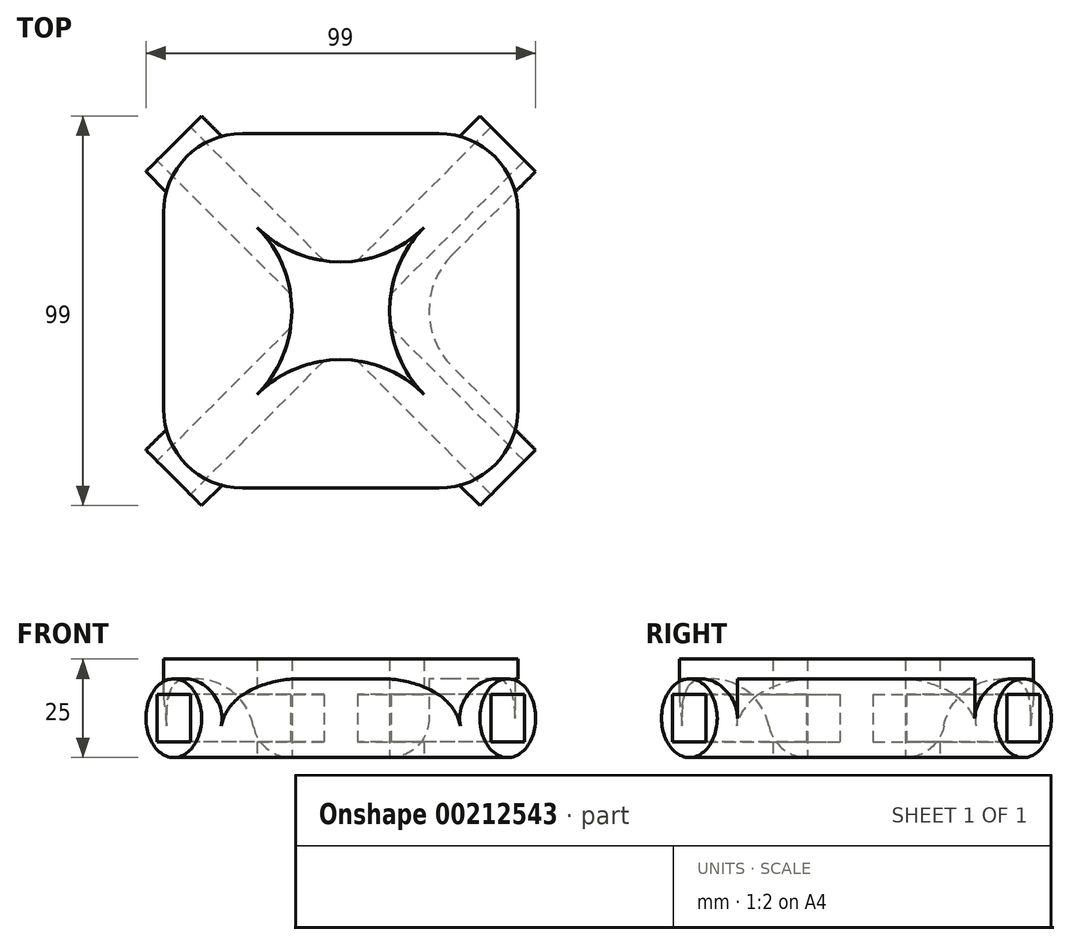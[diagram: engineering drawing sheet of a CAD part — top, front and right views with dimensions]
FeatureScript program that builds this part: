
annotation { "Feature Type Name" : "Feature", "Feature Type Description" : "" }
export const myFeature = defineFeature(function(context is Context, id is Id, definition is map)
    precondition{}
    {
        {
            var Q0;
            Q0=qCreatedBy(makeId("Top.planeOp"),FACE);
            var sketch = newSketch(context, id + "F0", { "sketchPlane" : qUnion([Q0])});
            skLineSegment(sketch, "E0.bottom", {"start": v(25, 45) * mm, "end": v(-25, 45) * mm});
            skLineSegment(sketch, "E0.top", {"start": v(25, -45) * mm, "end": v(-25, -45) * mm});
            skLineSegment(sketch, "E0.left", {"start": v(45, 25) * mm, "end": v(45, -25) * mm});
            skLineSegment(sketch, "E0.right", {"start": v(-45, 25) * mm, "end": v(-45, -25) * mm});
            skPoint(sketch, "E0.middle", {"position": v(0, 0) * mm});
            skPoint(sketch, "E1.visualSharp", {"position": v(-45, 45) * mm});
            skArc(sketch, "E1.filletArc", {"start": v(-25, 45) * mm, "mid": v(-39.14, 39.14) * mm, "end": v(-45, 25) * mm});
            skPoint(sketch, "E2.visualSharp", {"position": v(45, 45) * mm});
            skArc(sketch, "E2.filletArc", {"start": v(45, 25) * mm, "mid": v(39.14, 39.14) * mm, "end": v(25, 45) * mm});
            skPoint(sketch, "E3.visualSharp", {"position": v(45, -45) * mm});
            skArc(sketch, "E3.filletArc", {"start": v(25, -45) * mm, "mid": v(39.14, -39.14) * mm, "end": v(45, -25) * mm});
            skPoint(sketch, "E4.visualSharp", {"position": v(-45, -45) * mm});
            skArc(sketch, "E4.filletArc", {"start": v(-45, -25) * mm, "mid": v(-39.14, -39.14) * mm, "end": v(-25, -45) * mm});
            skSolve(sketch);
        }
        {
            var Q0;
            Q0=qCreatedBy(makeId("Top.planeOp"),FACE);
            cPlane(context, id + "F1", {"entities" : qUnion([Q0]), "cplaneType" : CPlaneType.OFFSET, "offset" : 20 * mm, "oppositeDirection" : true, "width" : 150 * mm, "height" : 150 * mm});
        }
        {
            var Q0;
            Q0=qCreatedBy(id+"F1.planeOp",FACE);
            var sketch = newSketch(context, id + "F2", { "sketchPlane" : qUnion([Q0])});
            skLineSegment(sketch, "E5", {"start": v(-42.43, -42.43) * mm, "end": v(42.43, 42.43) * mm, "construction": true});
            skLineSegment(sketch, "E6", {"start": v(-42.43, 42.43) * mm, "end": v(42.43, -42.43) * mm, "construction": true});
            skLineSegment(sketch, "E7", {"start": v(0, 0) * mm, "end": v(0, -45) * mm, "construction": true});
            skLineSegment(sketch, "E8.bottom", {"start": v(-49.5, -35.36) * mm, "end": v(-35.36, -49.5) * mm});
            skLineSegment(sketch, "E8.top", {"start": v(35.36, 49.5) * mm, "end": v(49.5, 35.36) * mm});
            skLineSegment(sketch, "E8.left", {"start": v(-49.5, -35.36) * mm, "end": v(-28.28, -14.14) * mm});
            skLineSegment(sketch, "E8.right", {"start": v(-35.36, -49.5) * mm, "end": v(-14.14, -28.28) * mm});
            skPoint(sketch, "E8.middle", {"position": v(0, 0) * mm});
            skLineSegment(sketch, "E9.bottom", {"start": v(49.5, -35.36) * mm, "end": v(28.28, -14.14) * mm});
            skLineSegment(sketch, "E9.top", {"start": v(35.36, -49.5) * mm, "end": v(14.14, -28.28) * mm});
            skLineSegment(sketch, "E9.left", {"start": v(35.36, -49.5) * mm, "end": v(49.5, -35.36) * mm});
            skLineSegment(sketch, "E9.right", {"start": v(-49.5, 35.36) * mm, "end": v(-35.36, 49.5) * mm});
            skLineSegment(sketch, "E10.trimOffspring", {"start": v(14.14, 28.28) * mm, "end": v(35.36, 49.5) * mm});
            skLineSegment(sketch, "E11.trimOffspring", {"start": v(-28.28, 14.14) * mm, "end": v(-49.5, 35.36) * mm});
            skLineSegment(sketch, "E12.trimOffspring", {"start": v(28.28, 14.14) * mm, "end": v(49.5, 35.36) * mm});
            skLineSegment(sketch, "E13.trimOffspring", {"start": v(-14.14, 28.28) * mm, "end": v(-35.36, 49.5) * mm});
            skPoint(sketch, "E14.visualSharp", {"position": v(0, -14.14) * mm});
            skArc(sketch, "E14.filletArc", {"start": v(14.14, -28.28) * mm, "mid": v(0, -22.43) * mm, "end": v(-14.14, -28.28) * mm});
            skPoint(sketch, "E15.visualSharp", {"position": v(-14.14, 0) * mm});
            skArc(sketch, "E15.filletArc", {"start": v(-28.28, -14.14) * mm, "mid": v(-22.43, 0) * mm, "end": v(-28.28, 14.14) * mm});
            skPoint(sketch, "E16.visualSharp", {"position": v(14.14, 0) * mm});
            skArc(sketch, "E16.filletArc", {"start": v(28.28, 14.14) * mm, "mid": v(22.43, 0) * mm, "end": v(28.28, -14.14) * mm});
            skPoint(sketch, "E17.visualSharp", {"position": v(0, 14.14) * mm});
            skArc(sketch, "E17.filletArc", {"start": v(-14.14, 28.28) * mm, "mid": v(0, 22.43) * mm, "end": v(14.14, 28.28) * mm});
            skSolve(sketch);
        }
        {
            var Q0;
            Q0=makeQuery(id+"F0.imprint","IMPRINT",FACE,{"disambiguationData":[TD([[makeQuery(id+"F0.imprint","IMPRINT",EDGE,{"derivedFrom":sQuery(id+"F0.wireOp",EDGE,"E0.bottom")}),1.0]])]});
            extrude(context, id + "F3", {"entities" : qUnion([Q0]), "depth" : 5 * mm});
        }
        {
            var Q0;
            Q0=makeQuery(id+"F2.imprint","IMPRINT",FACE,{"disambiguationData":[TD([[makeQuery(id+"F2.imprint","IMPRINT",EDGE,{"derivedFrom":sQuery(id+"F2.wireOp",EDGE,"E8.bottom")}),1.0]])]});
            var Q1;
            Q1=makeQuery(id+"F3.opExtrude","CAP_FACE",FACE,{"disambiguationData":[OSD([sQuery(id+"F0.wireOp",EDGE,"E0.bottom"),sQuery(id+"F0.wireOp",EDGE,"E0.top"),sQuery(id+"F0.wireOp",EDGE,"E0.left"),sQuery(id+"F0.wireOp",EDGE,"E0.right"),sQuery(id+"F0.wireOp",EDGE,"E1.filletArc"),sQuery(id+"F0.wireOp",EDGE,"E2.filletArc"),sQuery(id+"F0.wireOp",EDGE,"E3.filletArc"),sQuery(id+"F0.wireOp",EDGE,"E4.filletArc")])],"isStart":true});
            extrude(context, id + "F4", {"entities" : qUnion([Q0]), "operationType" : NewBodyOperationType.ADD, "endBound" : BoundingType.UP_TO_SURFACE, "endBoundEntityFace" : qUnion([Q1]), "depth" : 25 * mm});
        }
        {
            var Q0;
            Q0=makeQuery(id+"F4.opExtrude","CAP_EDGE",EDGE,{"disambiguationData":[OSD([sQuery(id+"F2.wireOp",EDGE,"E9.bottom")])],"isStart":true});
            var Q1;
            Q1=makeQuery(id+"F4.opExtrude","CAP_EDGE",EDGE,{"disambiguationData":[OSD([sQuery(id+"F2.wireOp",EDGE,"E14.filletArc")])],"isStart":true});
            var Q2;
            Q2=makeQuery(id+"F4.opExtrude","CAP_EDGE",EDGE,{"disambiguationData":[OSD([sQuery(id+"F2.wireOp",EDGE,"E15.filletArc")])],"isStart":true});
            var Q3;
            Q3=makeQuery(id+"F4.opExtrude","CAP_EDGE",EDGE,{"disambiguationData":[OSD([sQuery(id+"F2.wireOp",EDGE,"E17.filletArc")])],"isStart":true});
            fillet(context, id + "F5", {"entities" : qUnion([Q0, Q1, Q2, Q3]), "radius" : 10 * mm, "tangentPropagation" : true, "allowEdgeOverflow" : false});
        }
        {
            var Q0;
            {var subQ0=sQuery(id+"F2.wireOp",EDGE,"E12.trimOffspring");Q0=makeQuery(id+"F4.boolean.opBoolean","SPLIT",EDGE,{"disambiguationData":[topologyDisambiguationEdgeConnected([makeQuery(id+"F4.opExtrude","CAP_FACE",FACE,{"disambiguationData":[OSD([sQuery(id+"F2.wireOp",EDGE,"E8.bottom"),sQuery(id+"F2.wireOp",EDGE,"E8.top"),sQuery(id+"F2.wireOp",EDGE,"E8.left"),sQuery(id+"F2.wireOp",EDGE,"E8.right"),sQuery(id+"F2.wireOp",EDGE,"E9.bottom"),sQuery(id+"F2.wireOp",EDGE,"E9.top"),sQuery(id+"F2.wireOp",EDGE,"E9.left"),sQuery(id+"F2.wireOp",EDGE,"E9.right"),sQuery(id+"F2.wireOp",EDGE,"E10.trimOffspring"),sQuery(id+"F2.wireOp",EDGE,"E11.trimOffspring"),subQ0,sQuery(id+"F2.wireOp",EDGE,"E13.trimOffspring"),sQuery(id+"F2.wireOp",EDGE,"E14.filletArc"),sQuery(id+"F2.wireOp",EDGE,"E15.filletArc"),sQuery(id+"F2.wireOp",EDGE,"E16.filletArc"),sQuery(id+"F2.wireOp",EDGE,"E17.filletArc")])],"isStart":false})])],"derivedFrom":makeQuery(id+"F4.opExtrude","CAP_EDGE",EDGE,{"disambiguationData":[OSD([subQ0])],"isStart":false})});}
            var Q1;
            {var subQ0=sQuery(id+"F2.wireOp",EDGE,"E10.trimOffspring");Q1=makeQuery(id+"F4.boolean.opBoolean","SPLIT",EDGE,{"disambiguationData":[topologyDisambiguationEdgeConnected([makeQuery(id+"F4.opExtrude","CAP_FACE",FACE,{"disambiguationData":[OSD([sQuery(id+"F2.wireOp",EDGE,"E8.bottom"),sQuery(id+"F2.wireOp",EDGE,"E8.top"),sQuery(id+"F2.wireOp",EDGE,"E8.left"),sQuery(id+"F2.wireOp",EDGE,"E8.right"),sQuery(id+"F2.wireOp",EDGE,"E9.bottom"),sQuery(id+"F2.wireOp",EDGE,"E9.top"),sQuery(id+"F2.wireOp",EDGE,"E9.left"),sQuery(id+"F2.wireOp",EDGE,"E9.right"),subQ0,sQuery(id+"F2.wireOp",EDGE,"E11.trimOffspring"),sQuery(id+"F2.wireOp",EDGE,"E12.trimOffspring"),sQuery(id+"F2.wireOp",EDGE,"E13.trimOffspring"),sQuery(id+"F2.wireOp",EDGE,"E14.filletArc"),sQuery(id+"F2.wireOp",EDGE,"E15.filletArc"),sQuery(id+"F2.wireOp",EDGE,"E16.filletArc"),sQuery(id+"F2.wireOp",EDGE,"E17.filletArc")])],"isStart":false})])],"derivedFrom":makeQuery(id+"F4.opExtrude","CAP_EDGE",EDGE,{"disambiguationData":[OSD([subQ0])],"isStart":false})});}
            var Q2;
            {var subQ0=sQuery(id+"F2.wireOp",EDGE,"E13.trimOffspring");Q2=makeQuery(id+"F4.boolean.opBoolean","SPLIT",EDGE,{"disambiguationData":[topologyDisambiguationEdgeConnected([makeQuery(id+"F4.opExtrude","CAP_FACE",FACE,{"disambiguationData":[OSD([sQuery(id+"F2.wireOp",EDGE,"E8.bottom"),sQuery(id+"F2.wireOp",EDGE,"E8.top"),sQuery(id+"F2.wireOp",EDGE,"E8.left"),sQuery(id+"F2.wireOp",EDGE,"E8.right"),sQuery(id+"F2.wireOp",EDGE,"E9.bottom"),sQuery(id+"F2.wireOp",EDGE,"E9.top"),sQuery(id+"F2.wireOp",EDGE,"E9.left"),sQuery(id+"F2.wireOp",EDGE,"E9.right"),sQuery(id+"F2.wireOp",EDGE,"E10.trimOffspring"),sQuery(id+"F2.wireOp",EDGE,"E11.trimOffspring"),sQuery(id+"F2.wireOp",EDGE,"E12.trimOffspring"),subQ0,sQuery(id+"F2.wireOp",EDGE,"E14.filletArc"),sQuery(id+"F2.wireOp",EDGE,"E15.filletArc"),sQuery(id+"F2.wireOp",EDGE,"E16.filletArc"),sQuery(id+"F2.wireOp",EDGE,"E17.filletArc")])],"isStart":false})])],"derivedFrom":makeQuery(id+"F4.opExtrude","CAP_EDGE",EDGE,{"disambiguationData":[OSD([subQ0])],"isStart":false})});}
            var Q3;
            {var subQ0=sQuery(id+"F2.wireOp",EDGE,"E11.trimOffspring");Q3=makeQuery(id+"F4.boolean.opBoolean","SPLIT",EDGE,{"disambiguationData":[topologyDisambiguationEdgeConnected([makeQuery(id+"F4.opExtrude","CAP_FACE",FACE,{"disambiguationData":[OSD([sQuery(id+"F2.wireOp",EDGE,"E8.bottom"),sQuery(id+"F2.wireOp",EDGE,"E8.top"),sQuery(id+"F2.wireOp",EDGE,"E8.left"),sQuery(id+"F2.wireOp",EDGE,"E8.right"),sQuery(id+"F2.wireOp",EDGE,"E9.bottom"),sQuery(id+"F2.wireOp",EDGE,"E9.top"),sQuery(id+"F2.wireOp",EDGE,"E9.left"),sQuery(id+"F2.wireOp",EDGE,"E9.right"),sQuery(id+"F2.wireOp",EDGE,"E10.trimOffspring"),subQ0,sQuery(id+"F2.wireOp",EDGE,"E12.trimOffspring"),sQuery(id+"F2.wireOp",EDGE,"E13.trimOffspring"),sQuery(id+"F2.wireOp",EDGE,"E14.filletArc"),sQuery(id+"F2.wireOp",EDGE,"E15.filletArc"),sQuery(id+"F2.wireOp",EDGE,"E16.filletArc"),sQuery(id+"F2.wireOp",EDGE,"E17.filletArc")])],"isStart":false})])],"derivedFrom":makeQuery(id+"F4.opExtrude","CAP_EDGE",EDGE,{"disambiguationData":[OSD([subQ0])],"isStart":false})});}
            var Q4;
            {var subQ0=sQuery(id+"F2.wireOp",EDGE,"E8.left");Q4=makeQuery(id+"F4.boolean.opBoolean","SPLIT",EDGE,{"disambiguationData":[topologyDisambiguationEdgeConnected([makeQuery(id+"F4.opExtrude","CAP_FACE",FACE,{"disambiguationData":[OSD([sQuery(id+"F2.wireOp",EDGE,"E8.bottom"),sQuery(id+"F2.wireOp",EDGE,"E8.top"),subQ0,sQuery(id+"F2.wireOp",EDGE,"E8.right"),sQuery(id+"F2.wireOp",EDGE,"E9.bottom"),sQuery(id+"F2.wireOp",EDGE,"E9.top"),sQuery(id+"F2.wireOp",EDGE,"E9.left"),sQuery(id+"F2.wireOp",EDGE,"E9.right"),sQuery(id+"F2.wireOp",EDGE,"E10.trimOffspring"),sQuery(id+"F2.wireOp",EDGE,"E11.trimOffspring"),sQuery(id+"F2.wireOp",EDGE,"E12.trimOffspring"),sQuery(id+"F2.wireOp",EDGE,"E13.trimOffspring"),sQuery(id+"F2.wireOp",EDGE,"E14.filletArc"),sQuery(id+"F2.wireOp",EDGE,"E15.filletArc"),sQuery(id+"F2.wireOp",EDGE,"E16.filletArc"),sQuery(id+"F2.wireOp",EDGE,"E17.filletArc")])],"isStart":false})])],"derivedFrom":makeQuery(id+"F4.opExtrude","CAP_EDGE",EDGE,{"disambiguationData":[OSD([subQ0])],"isStart":false})});}
            var Q5;
            {var subQ0=sQuery(id+"F2.wireOp",EDGE,"E8.right");Q5=makeQuery(id+"F4.boolean.opBoolean","SPLIT",EDGE,{"disambiguationData":[topologyDisambiguationEdgeConnected([makeQuery(id+"F4.opExtrude","CAP_FACE",FACE,{"disambiguationData":[OSD([sQuery(id+"F2.wireOp",EDGE,"E8.bottom"),sQuery(id+"F2.wireOp",EDGE,"E8.top"),sQuery(id+"F2.wireOp",EDGE,"E8.left"),subQ0,sQuery(id+"F2.wireOp",EDGE,"E9.bottom"),sQuery(id+"F2.wireOp",EDGE,"E9.top"),sQuery(id+"F2.wireOp",EDGE,"E9.left"),sQuery(id+"F2.wireOp",EDGE,"E9.right"),sQuery(id+"F2.wireOp",EDGE,"E10.trimOffspring"),sQuery(id+"F2.wireOp",EDGE,"E11.trimOffspring"),sQuery(id+"F2.wireOp",EDGE,"E12.trimOffspring"),sQuery(id+"F2.wireOp",EDGE,"E13.trimOffspring"),sQuery(id+"F2.wireOp",EDGE,"E14.filletArc"),sQuery(id+"F2.wireOp",EDGE,"E15.filletArc"),sQuery(id+"F2.wireOp",EDGE,"E16.filletArc"),sQuery(id+"F2.wireOp",EDGE,"E17.filletArc")])],"isStart":false})])],"derivedFrom":makeQuery(id+"F4.opExtrude","CAP_EDGE",EDGE,{"disambiguationData":[OSD([subQ0])],"isStart":false})});}
            var Q6;
            {var subQ0=sQuery(id+"F2.wireOp",EDGE,"E9.top");Q6=makeQuery(id+"F4.boolean.opBoolean","SPLIT",EDGE,{"disambiguationData":[topologyDisambiguationEdgeConnected([makeQuery(id+"F4.opExtrude","CAP_FACE",FACE,{"disambiguationData":[OSD([sQuery(id+"F2.wireOp",EDGE,"E8.bottom"),sQuery(id+"F2.wireOp",EDGE,"E8.top"),sQuery(id+"F2.wireOp",EDGE,"E8.left"),sQuery(id+"F2.wireOp",EDGE,"E8.right"),sQuery(id+"F2.wireOp",EDGE,"E9.bottom"),subQ0,sQuery(id+"F2.wireOp",EDGE,"E9.left"),sQuery(id+"F2.wireOp",EDGE,"E9.right"),sQuery(id+"F2.wireOp",EDGE,"E10.trimOffspring"),sQuery(id+"F2.wireOp",EDGE,"E11.trimOffspring"),sQuery(id+"F2.wireOp",EDGE,"E12.trimOffspring"),sQuery(id+"F2.wireOp",EDGE,"E13.trimOffspring"),sQuery(id+"F2.wireOp",EDGE,"E14.filletArc"),sQuery(id+"F2.wireOp",EDGE,"E15.filletArc"),sQuery(id+"F2.wireOp",EDGE,"E16.filletArc"),sQuery(id+"F2.wireOp",EDGE,"E17.filletArc")])],"isStart":false})])],"derivedFrom":makeQuery(id+"F4.opExtrude","CAP_EDGE",EDGE,{"disambiguationData":[OSD([subQ0])],"isStart":false})});}
            var Q7;
            {var subQ0=sQuery(id+"F2.wireOp",EDGE,"E9.bottom");Q7=makeQuery(id+"F4.boolean.opBoolean","SPLIT",EDGE,{"disambiguationData":[topologyDisambiguationEdgeConnected([makeQuery(id+"F4.opExtrude","CAP_FACE",FACE,{"disambiguationData":[OSD([sQuery(id+"F2.wireOp",EDGE,"E8.bottom"),sQuery(id+"F2.wireOp",EDGE,"E8.top"),sQuery(id+"F2.wireOp",EDGE,"E8.left"),sQuery(id+"F2.wireOp",EDGE,"E8.right"),subQ0,sQuery(id+"F2.wireOp",EDGE,"E9.top"),sQuery(id+"F2.wireOp",EDGE,"E9.left"),sQuery(id+"F2.wireOp",EDGE,"E9.right"),sQuery(id+"F2.wireOp",EDGE,"E10.trimOffspring"),sQuery(id+"F2.wireOp",EDGE,"E11.trimOffspring"),sQuery(id+"F2.wireOp",EDGE,"E12.trimOffspring"),sQuery(id+"F2.wireOp",EDGE,"E13.trimOffspring"),sQuery(id+"F2.wireOp",EDGE,"E14.filletArc"),sQuery(id+"F2.wireOp",EDGE,"E15.filletArc"),sQuery(id+"F2.wireOp",EDGE,"E16.filletArc"),sQuery(id+"F2.wireOp",EDGE,"E17.filletArc")])],"isStart":false})])],"derivedFrom":makeQuery(id+"F4.opExtrude","CAP_EDGE",EDGE,{"disambiguationData":[OSD([subQ0])],"isStart":false})});}
            fillet(context, id + "F6", {"entities" : qUnion([Q0, Q1, Q2, Q3, Q4, Q5, Q6, Q7]), "radius" : 10 * mm, "tangentPropagation" : true, "allowEdgeOverflow" : false});
        }
        {
            var Q0;
            Q0=makeQuery(id+"F4.opExtrude","CAP_EDGE",EDGE,{"disambiguationData":[OSD([sQuery(id+"F2.wireOp",EDGE,"E14.filletArc")])],"isStart":false});
            var Q1;
            Q1=makeQuery(id+"F4.opExtrude","CAP_EDGE",EDGE,{"disambiguationData":[OSD([sQuery(id+"F2.wireOp",EDGE,"E16.filletArc")])],"isStart":false});
            var Q2;
            Q2=makeQuery(id+"F4.opExtrude","CAP_EDGE",EDGE,{"disambiguationData":[OSD([sQuery(id+"F2.wireOp",EDGE,"E15.filletArc")])],"isStart":false});
            var Q3;
            Q3=makeQuery(id+"F4.opExtrude","CAP_EDGE",EDGE,{"disambiguationData":[OSD([sQuery(id+"F2.wireOp",EDGE,"E17.filletArc")])],"isStart":false});
            fillet(context, id + "F7", {"entities" : qUnion([Q0, Q1, Q2, Q3]), "radius" : 15 * mm, "tangentPropagation" : true, "allowEdgeOverflow" : false});
        }
        {
            var Q0;
            Q0=makeQuery(id+"F4.opExtrude","CAP_FACE",FACE,{"disambiguationData":[OSD([sQuery(id+"F2.wireOp",EDGE,"E8.bottom"),sQuery(id+"F2.wireOp",EDGE,"E8.top"),sQuery(id+"F2.wireOp",EDGE,"E8.left"),sQuery(id+"F2.wireOp",EDGE,"E8.right"),sQuery(id+"F2.wireOp",EDGE,"E9.bottom"),sQuery(id+"F2.wireOp",EDGE,"E9.top"),sQuery(id+"F2.wireOp",EDGE,"E9.left"),sQuery(id+"F2.wireOp",EDGE,"E9.right"),sQuery(id+"F2.wireOp",EDGE,"E10.trimOffspring"),sQuery(id+"F2.wireOp",EDGE,"E11.trimOffspring"),sQuery(id+"F2.wireOp",EDGE,"E12.trimOffspring"),sQuery(id+"F2.wireOp",EDGE,"E13.trimOffspring"),sQuery(id+"F2.wireOp",EDGE,"E14.filletArc"),sQuery(id+"F2.wireOp",EDGE,"E15.filletArc"),sQuery(id+"F2.wireOp",EDGE,"E16.filletArc"),sQuery(id+"F2.wireOp",EDGE,"E17.filletArc")])],"isStart":true});
            extrude(context, id + "F8", {"entities" : qUnion([Q0]), "operationType" : NewBodyOperationType.REMOVE, "endBound" : BoundingType.THROUGH_ALL, "oppositeDirection" : true, "depth" : 25 * mm});
        }
        {
            var Q0;
            Q0=makeQuery(id+"F4.opExtrude","SWEPT_FACE",FACE,{"disambiguationData":[OSD([sQuery(id+"F2.wireOp",EDGE,"E9.right")])]});
            var sketch = newSketch(context, id + "F9", { "sketchPlane" : qUnion([Q0])});
            skLineSegment(sketch, "E18.bottom", {"start": v(6, -4) * mm, "end": v(-6, -4) * mm});
            skLineSegment(sketch, "E18.top", {"start": v(6, -16) * mm, "end": v(-6, -16) * mm});
            skLineSegment(sketch, "E18.left", {"start": v(6, -4) * mm, "end": v(6, -16) * mm});
            skLineSegment(sketch, "E18.right", {"start": v(-6, -4) * mm, "end": v(-6, -16) * mm});
            skPoint(sketch, "E18.middle", {"position": v(0, -10) * mm});
            skSolve(sketch);
        }
        {
            var Q0;
            Q0=makeQuery(id+"F9.imprint","IMPRINT",FACE,{"disambiguationData":[TD([[makeQuery(id+"F9.imprint","IMPRINT",EDGE,{"derivedFrom":sQuery(id+"F9.wireOp",EDGE,"E18.bottom")}),1.0]])]});
            extrude(context, id + "F10", {"entities" : qUnion([Q0]), "operationType" : NewBodyOperationType.REMOVE, "endBound" : BoundingType.THROUGH_ALL, "oppositeDirection" : true, "depth" : 25 * mm});
        }
        {
            var Q0;
            Q0=makeQuery(id+"F4.opExtrude","SWEPT_FACE",FACE,{"disambiguationData":[OSD([sQuery(id+"F2.wireOp",EDGE,"E8.bottom")])]});
            var sketch = newSketch(context, id + "F11", { "sketchPlane" : qUnion([Q0])});
            skLineSegment(sketch, "E19.bottom", {"start": v(6, -4) * mm, "end": v(-6, -4) * mm});
            skLineSegment(sketch, "E19.top", {"start": v(6, -16) * mm, "end": v(-6, -16) * mm});
            skLineSegment(sketch, "E19.left", {"start": v(6, -4) * mm, "end": v(6, -16) * mm});
            skLineSegment(sketch, "E19.right", {"start": v(-6, -4) * mm, "end": v(-6, -16) * mm});
            skPoint(sketch, "E19.middle", {"position": v(0, -10) * mm});
            skSolve(sketch);
        }
        {
            var Q0;
            Q0=makeQuery(id+"F11.imprint","IMPRINT",FACE,{"disambiguationData":[TD([[makeQuery(id+"F11.imprint","IMPRINT",EDGE,{"derivedFrom":sQuery(id+"F11.wireOp",EDGE,"E19.bottom")}),1.0]])]});
            extrude(context, id + "F12", {"entities" : qUnion([Q0]), "operationType" : NewBodyOperationType.REMOVE, "endBound" : BoundingType.THROUGH_ALL, "oppositeDirection" : true, "depth" : 25 * mm});
        }
    });
